# Revit family: BLS-10 & 8A
name_source: partatom
category: Lighting Fixtures
units: mm (PartAtom-declared; Revit-internal decimal feet)

## family parameters
Cut with Voids When Loaded = No
Host = Face
Light Source = Yes
Maintain Annotation Orientation = No
Part Type = Normal
Room Calculation Point = No
Round Connector Dimension = Use Diameter
Shared = No

## types (2) — shared parameters
Color Filter = 16777215
Default Elevation = 4 '
Dimming Lamp Color Temperature Shift = <None>
Emit from Line Length = 2 '
Keynote = LUCE SOLARE
Lamp = LED
Manufacturer = BEGHELLI
POLE HEIGHT = 5 '
POLE MATERIAL = BRACKET
Tilt Angle = 60.00°
Type Image = BLS-8A IMAGE.PNG

## per-type parameters (varying)
| type | Description | Photometric Web File | Type Comments | Wattage Comments |
| BLS-8A | The LUCE SOLARE BLS-8A is a solar street and area lighting 
solution that integrates the solar panel, battery and LED module 
into a single low-profile fixture. BLS-8A utilitizes battery 
technology that will not drain below 10% capacity to 
ensure reliable re-charge for maximum performance. | BLS-8A-5700°K.ies | APPLICATION: The BLS-8A is ideal for temporary lighting, 
pathways, parking areas, public walkways, parks and roads.
SPECIFICATIONS
Solar Panel 75W, 16.2V
LI-ION Battery 577.2 Wh, 39 Ah, 14.8V
Lumen Output
3030 LEDS 180-190lpw @ 150mA, 5.8-6V
Operation Time 36 hrs (after full charge)
Discharge Time
Discharge Operating Temperature -20° to 60°C (-4° to 140°F)
Charge Time 10-12 hrs minimum
Charge Operating Temperature 0° to 60°C ( 32° to 140°F)
Min. Solar Direct Normal Irradiance 0.2 KWh/m2
Operation Mode (Green Light) 5 hrs @ 100% + 7 hrs @ 30%
(+ PIR 100%)
Operation Mode (Orange Light) 5 hrs @ 70% + 7 hrs @ 30%
(+ PIR 100%)
Operation Mode (Red Light) 12 hrs @ 30% (+ PIR 100%)
Mounting Height 19 - 26 ft
Effective Projected Area (EPA) 6.4 ft2
Certifications IP65 / ROHS / FCC
Weight 45.0 lb / 20.4 kg
Warranty 3 years
Upon proper installation and start-up, Beghelli does not guarantee product performance meets specified performance levels. Unknown 
environmental conditions effect performance. In no event shall Beghelli be liable for special, incidental or consequential damages related directly or 
indirectly to the lack of product functionality and / or performance. 
ADVANTAGES
• Integrated Solution
• Environmentally Friendly
• Easy Installation
• $0 Energy Costs
• PIR Motion Sensor
• 3 Lighting Modes
EXTRUDED ALUMINUM FRAMING 
WITH CLEAR ANODIZED FINISH
SOLAR PANEL - 75W
OPERATION MODES SWITCH
(on/ off- depress long 1.5 sec)
61.5"
15"
381 mm
1563 mm
OPERATION MODES 
LIGHT INDICATOR
FABRICATED STEEL POST TOP MOUNTING 
BRACKET WITH GRAY PAINTED FINISH
160 MID POWER LED
PIR MOTION SENSOR
SLIP-FIT FOR 2.75" O.D 
X 5" LONG TENON
2.75" O.D X 5" TENON/
POLE (BY OTHERS)
BATTERY
6518 lm @ 5700°K
1
 (5 SCDM)
(2)
SET SCREWS (PROVIDED)
BLS-8A
Type II / B2-U1-G1
System Power Delivery 45.3W
The LUCE SOLARE BLS-8A is a solar street and area lighting 
solution that integrates the solar panel, battery and LED module 
into a single low-profile fixture. BLS-8A utilitizes battery 
technology that will not drain below 10% capacity to 
ensure reliable re-charge for maximum performance.
The BLS-8A design eliminates bulky external battery 
boxes, while maximizing light output by using high 
efficiency mono-crystalline silicon solar cells and LEDs.
The BLS-8A incorporates a night sensor that detects 
ambient light to automatically turn the fixture on/off. An 
i | 45.3 |
| BLS-10A | APPLICATION: The BLS-10A is ideal for temporary lighting, 
pathways, parking areas, public walkways, parks and roads.
solution that integrates the solar panel, battery and LED module 
into a single low-profile fixture. BLS-8A utilitizes battery 
technology that will not drain below 10% capacity to 
ensure reliable re-charge for maximum performance. | BLS-10A-5700°K.ies | APPLICATION: The BLS-8A is ideal for temporary lighting, 
The LUCE SOLARE BLS-10A is a solar street and area lighting 
solution that integrates the solar panel, battery and LED module 
into a single low-profile fixture. BLS-10A utilitizes battery 
technology that will not drain below 10% capacity to ensure 
reliablere-chargefor maximum performance.
(+ PIR 100%)
Operation Mode (Orange Light) 5 hrs @ 70% + 7 hrs @ 30%
(+ PIR 100%)
Operation Mode (Red Light) 12 hrs @ 30% (+ PIR 100%)
Mounting Height 19 - 26 ft
Effective Projected Area (EPA) 6.4 ft2
Certifications IP65 / ROHS / FCC
Weight 45.0 lb / 20.4 kg
Warranty 3 years
Upon proper installation and start-up, Beghelli does not guarantee product performance meets specified performance levels. Unknown 
environmental conditions effect performance. In no event shall Beghelli be liable for special, incidental or consequential damages related directly or 
indirectly to the lack of product functionality and / or performance. 
ADVANTAGES
• Integrated Solution
• Environmentally Friendly
• Easy Installation
• $0 Energy Costs
• PIR Motion Sensor
• 3 Lighting Modes
EXTRUDED ALUMINUM FRAMING 
WITH CLEAR ANODIZED FINISH
SOLAR PANEL - 75W
OPERATION MODES SWITCH
(on/ off- depress long 1.5 sec)
61.5"
15"
381 mm
1563 mm
OPERATION MODES 
LIGHT INDICATOR
FABRICATED STEEL POST TOP MOUNTING 
BRACKET WITH GRAY PAINTED FINISH
160 MID POWER LED
PIR MOTION SENSOR
SLIP-FIT FOR 2.75" O.D 
X 5" LONG TENON
2.75" O.D X 5" TENON/
POLE (BY OTHERS)
BATTERY
6518 lm @ 5700°K
1
 (5 SCDM)
(2)
SET SCREWS (PROVIDED)
BLS-8A
Type II / B2-U1-G1
System Power Delivery 45.3W
The LUCE SOLARE BLS-8A is a solar street and area lighting 
solution that integrates the solar panel, battery and LED module 
into a single low-profile fixture. BLS-8A utilitizes battery 
technology that will not drain below 10% capacity to 
ensure reliable re-charge for maximum performance.
The BLS-8A design eliminates bulky external battery 
boxes, while maximizing light output by using high 
efficiency mono-crystalline silicon solar cells and LEDs.
The BLS-8A incorporates a night sensor that detects 
ambient light to automatically turn the fixture on/off. An 
i | 56.6 |

note: column(s) folded — value = type name in every type: Model

## geometry (parser evidence)
native form markers: Sweep x15
no freeform markers — native parametric forms only
